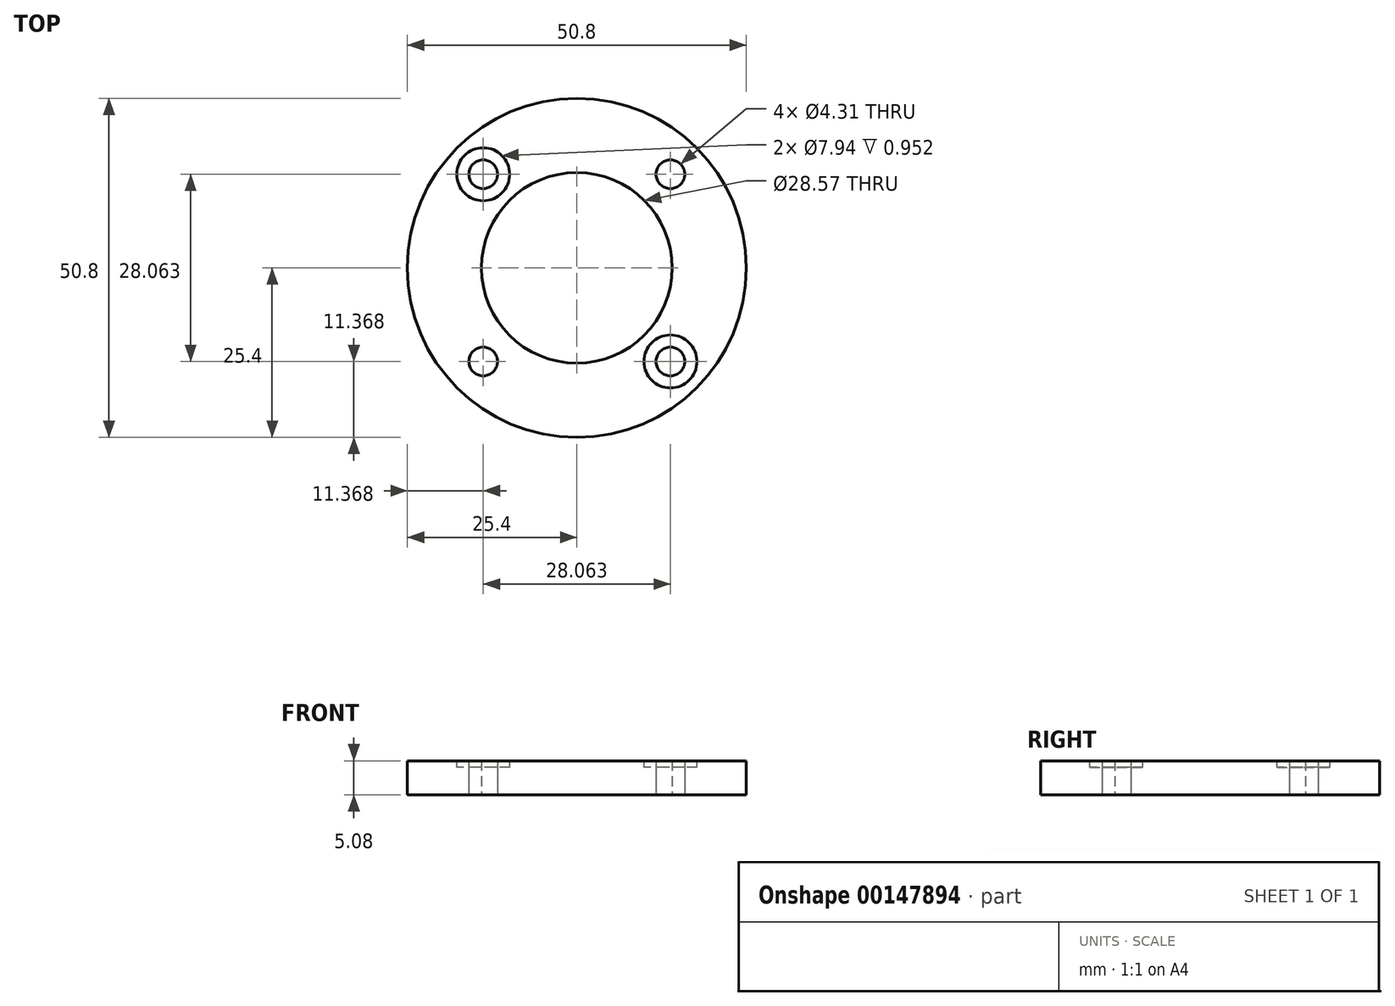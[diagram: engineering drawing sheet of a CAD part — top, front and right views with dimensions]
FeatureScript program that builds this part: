
annotation { "Feature Type Name" : "Feature", "Feature Type Description" : "" }
export const myFeature = defineFeature(function(context is Context, id is Id, definition is map)
    precondition{}
    {
        {
            var Q0;
            Q0=qCreatedBy(makeId("Top.planeOp"),FACE);
            var sketch = newSketch(context, id + "F0", { "sketchPlane" : qUnion([Q0])});
            skCircle(sketch, "E0", {"center": v(0, 0) * mm, "radius": 25.4 * mm});
            skCircle(sketch, "E1", {"center": v(0, 0) * mm, "radius": 14.29 * mm});
            skLineSegment(sketch, "E2.bottom", {"start": v(-14.03, -14.03) * mm, "end": v(14.03, -14.03) * mm, "construction": true});
            skLineSegment(sketch, "E2.top", {"start": v(-14.03, 14.03) * mm, "end": v(14.03, 14.03) * mm, "construction": true});
            skLineSegment(sketch, "E2.left", {"start": v(-14.03, -14.03) * mm, "end": v(-14.03, 14.03) * mm, "construction": true});
            skLineSegment(sketch, "E2.right", {"start": v(14.03, -14.03) * mm, "end": v(14.03, 14.03) * mm, "construction": true});
            skCircle(sketch, "E3", {"center": v(-14.03, -14.03) * mm, "radius": 5.56 * mm, "construction": true});
            skCircle(sketch, "E4", {"center": v(-14.03, -14.03) * mm, "radius": 2.15 * mm});
            skCircle(sketch, "E5", {"center": v(14.03, 14.03) * mm, "radius": 2.15 * mm});
            skCircle(sketch, "E6", {"center": v(14.03, -14.03) * mm, "radius": 2.15 * mm});
            skCircle(sketch, "E7", {"center": v(-14.03, 14.03) * mm, "radius": 2.15 * mm});
            skSolve(sketch);
        }
        {
            var Q0;
            Q0=makeQuery(id+"F0.imprint","IMPRINT",FACE,{"disambiguationData":[TD([[makeQuery(id+"F0.imprint","IMPRINT",EDGE,{"derivedFrom":sQuery(id+"F0.wireOp",EDGE,"d7zeTPih-CRss-xDOh-gPdP-rmPCdwzH7cdN.left")}),1.0]])]});
            var Q1;
            Q1=makeQuery(id+"F0.imprint","IMPRINT",FACE,{"disambiguationData":[TD([[makeQuery(id+"F0.imprint","IMPRINT",EDGE,{"derivedFrom":sQuery(id+"F0.wireOp",EDGE,"E0")}),1.0]])]});
            extrude(context, id + "F1", {"entities" : qUnion([Q0, Q1]), "depth" : 5.08 * mm});
        }
        {
            var Q0;
            Q0=makeQuery(id+"F1.opExtrude","CAP_FACE",FACE,{"disambiguationData":[OSD([sQuery(id+"F0.wireOp",EDGE,"E0"),sQuery(id+"F0.wireOp",EDGE,"E1"),sQuery(id+"F0.wireOp",EDGE,"E4"),sQuery(id+"F0.wireOp",EDGE,"E5"),sQuery(id+"F0.wireOp",EDGE,"E6"),sQuery(id+"F0.wireOp",EDGE,"E7")])],"isStart":false});
            var sketch = newSketch(context, id + "F2", { "sketchPlane" : qUnion([Q0])});
            skCircle(sketch, "E8", {"center": v(-14.03, 14.03) * mm, "radius": 3.97 * mm});
            skCircle(sketch, "E9", {"center": v(14.03, -14.03) * mm, "radius": 3.97 * mm});
            skSolve(sketch);
        }
        {
            var Q0;
            Q0=qSketchRegion(id+"F2",true);
            extrude(context, id + "F3", {"entities" : qUnion([Q0]), "operationType" : NewBodyOperationType.REMOVE, "oppositeDirection" : true, "depth" : 0.95 * mm});
        }
    });
